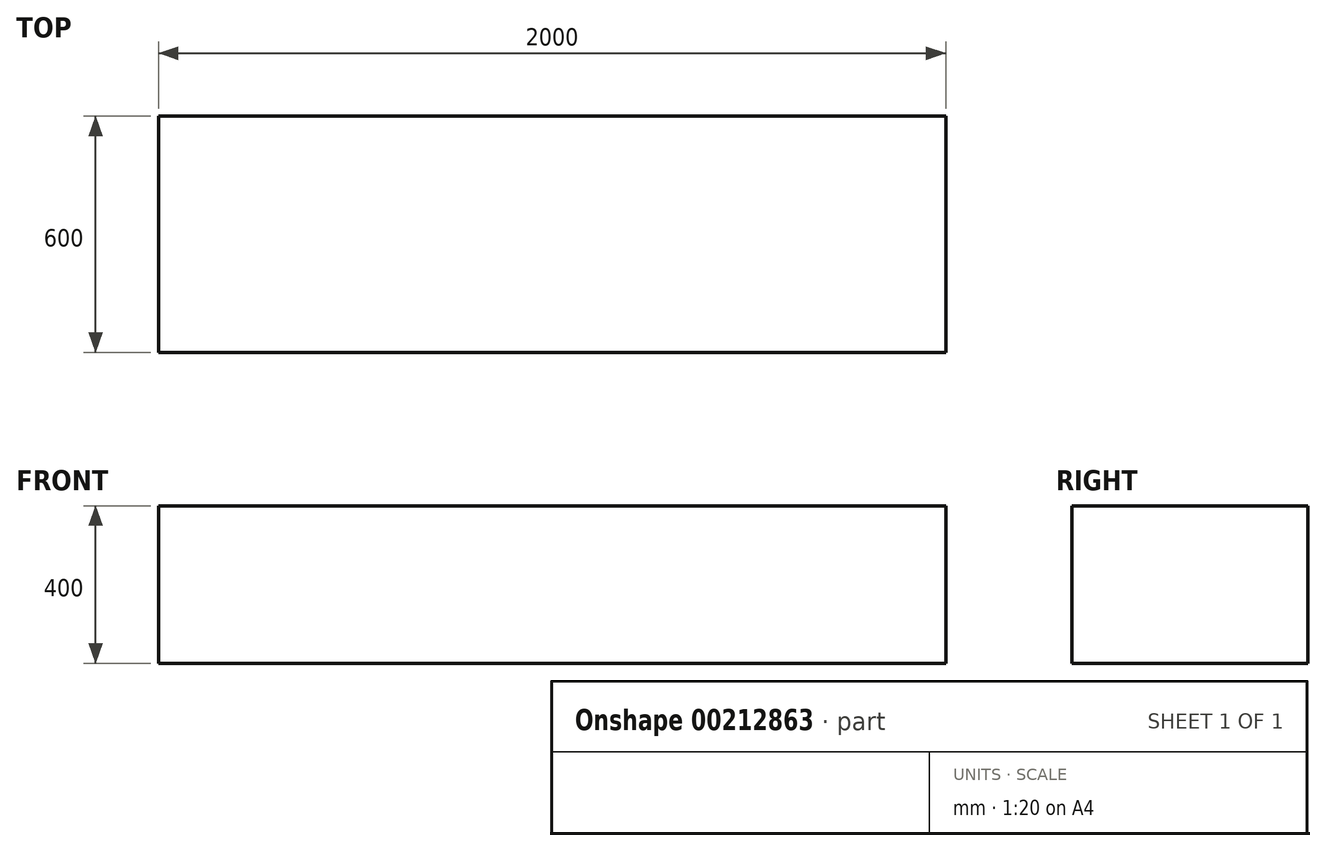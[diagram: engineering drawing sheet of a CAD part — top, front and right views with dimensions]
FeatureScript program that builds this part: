
annotation { "Feature Type Name" : "Feature", "Feature Type Description" : "" }
export const myFeature = defineFeature(function(context is Context, id is Id, definition is map)
    precondition{}
    {
        {
            var Q0;
            Q0=qCreatedBy(makeId("Top.planeOp"),FACE);
            var sketch = newSketch(context, id + "F0", { "sketchPlane" : qUnion([Q0])});
            skLineSegment(sketch, "E0.bottom", {"start": v(0, 0) * mm, "end": v(2000, 0) * mm});
            skLineSegment(sketch, "E0.top", {"start": v(0, 600) * mm, "end": v(2000, 600) * mm});
            skLineSegment(sketch, "E0.left", {"start": v(0, 0) * mm, "end": v(0, 600) * mm});
            skLineSegment(sketch, "E0.right", {"start": v(2000, 0) * mm, "end": v(2000, 600) * mm});
            skSolve(sketch);
        }
        {
            var Q0;
            Q0 = qSketchRegion(id + "F0", true);
            extrude(context, id + "F1", {"entities" : qUnion([Q0]), "depth" : 400 * mm});
        }
    });
